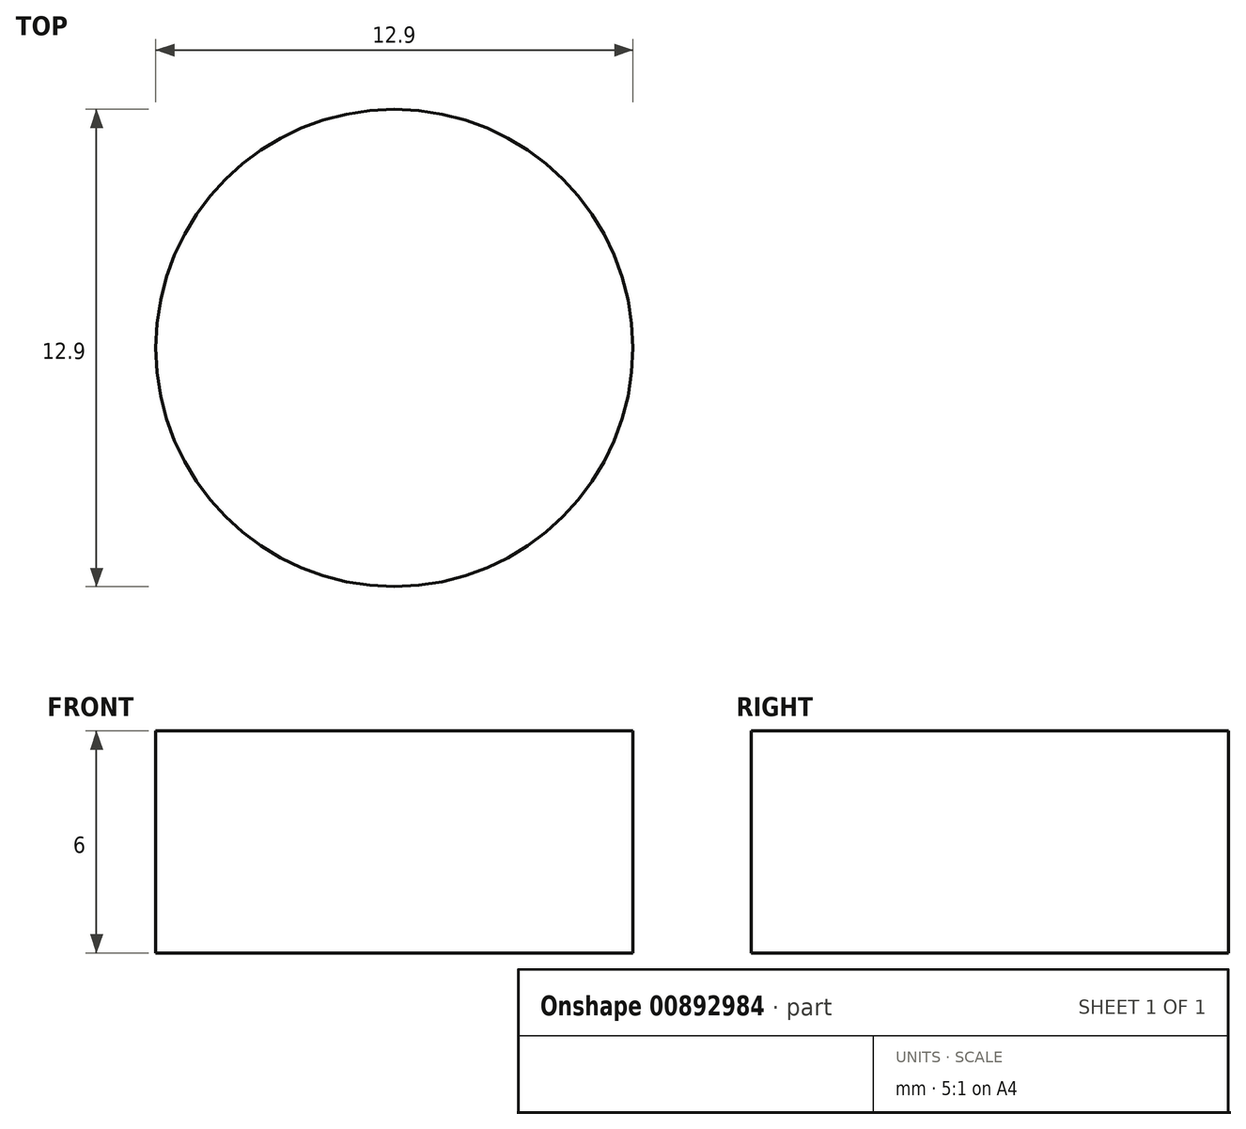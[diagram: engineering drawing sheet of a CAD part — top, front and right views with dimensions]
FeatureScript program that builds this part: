
annotation { "Feature Type Name" : "Feature", "Feature Type Description" : "" }
export const myFeature = defineFeature(function(context is Context, id is Id, definition is map)
    precondition{}
    {
        {
            var Q0;
            Q0=qCreatedBy(makeId("Top.planeOp"),FACE);
            var sketch = newSketch(context, id + "F0", { "sketchPlane" : qUnion([Q0])});
            skCircle(sketch, "E0", {"center": v(0, 0) * mm, "radius": 6.45 * mm});
            skSolve(sketch);
        }
        {
            var Q0;
            Q0=makeQuery(id+"F0.imprint","IMPRINT",FACE,{"disambiguationData":[TD([[makeQuery(id+"F0.imprint","IMPRINT",EDGE,{"derivedFrom":sQuery(id+"F0.wireOp",EDGE,"E0")}),1.0]])]});
            extrude(context, id + "F1", {"entities" : qUnion([Q0]), "depth" : 6 * mm, "offsetDistance" : 25 * mm});
        }
    });
